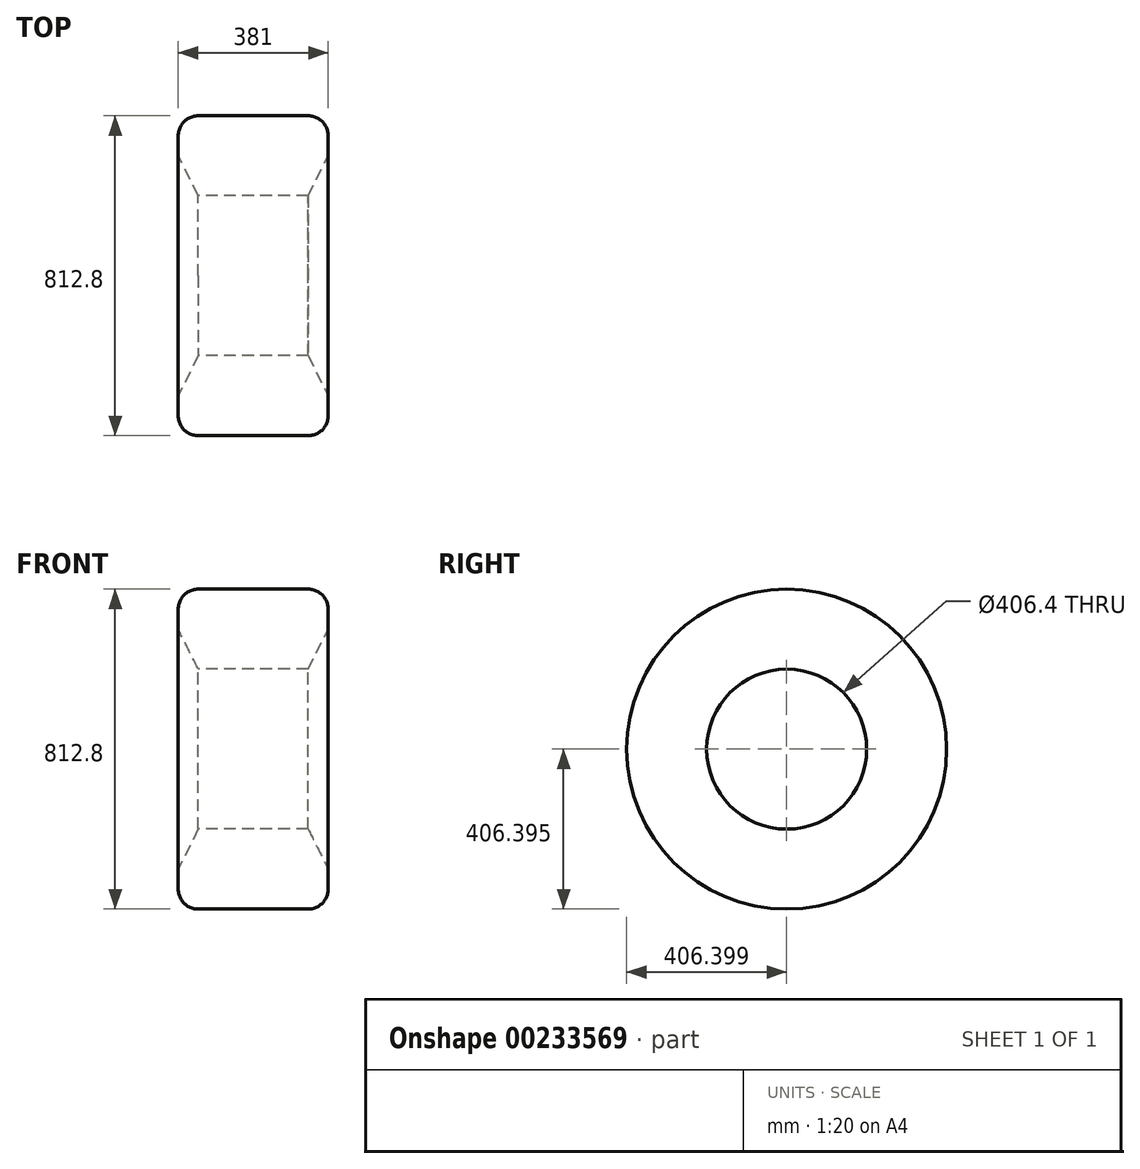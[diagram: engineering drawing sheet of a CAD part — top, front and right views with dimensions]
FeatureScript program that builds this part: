
annotation { "Feature Type Name" : "Feature", "Feature Type Description" : "" }
export const myFeature = defineFeature(function(context is Context, id is Id, definition is map)
    precondition{}
    {
        {
            var Q0;
            Q0=qCreatedBy(makeId("Right.planeOp"),FACE);
            var sketch = newSketch(context, id + "F0", { "sketchPlane" : qUnion([Q0])});
            skCircle(sketch, "E0", {"center": v(-535.52, 357.45) * mm, "radius": 406.4 * mm});
            skCircle(sketch, "E1", {"center": v(-535.52, 357.45) * mm, "radius": 203.2 * mm});
            skLineSegment(sketch, "E2", {"start": v(-535.52, 357.45) * mm, "end": v(-535.52, 763.85) * mm});
            skSolve(sketch);
        }
        {
            var Q0;
            Q0=makeQuery(id+"F0.imprint","IMPRINT",FACE,{"disambiguationData":[TD([[makeQuery(id+"F0.imprint","IMPRINT",EDGE,{"derivedFrom":sQuery(id+"F0.wireOp",EDGE,"E0")}),1.0]])]});
            extrude(context, id + "F1", {"entities" : qUnion([Q0]), "depth" : 381 * mm});
        }
        {
            var Q0;
            Q0=makeQuery(id+"F1.opExtrude","CAP_EDGE",EDGE,{"disambiguationData":[OSD([sQuery(id+"F0.wireOp",EDGE,"E0")])],"isStart":false});
            var Q1;
            Q1=makeQuery(id+"F1.opExtrude","CAP_EDGE",EDGE,{"disambiguationData":[OSD([sQuery(id+"F0.wireOp",EDGE,"E0")])],"isStart":true});
            fillet(context, id + "F2", {"entities" : qUnion([Q0, Q1]), "radius" : 50.8 * mm, "tangentPropagation" : true, "allowEdgeOverflow" : false});
        }
        {
            var Q0;
            Q0=makeQuery(id+"F1.opExtrude","CAP_FACE",FACE,{"disambiguationData":[OSD([sQuery(id+"F0.wireOp",EDGE,"E0"),sQuery(id+"F0.wireOp",EDGE,"E1")])],"isStart":false});
            chamfer(context, id + "F3", {"entities" : qUnion([Q0]), "chamferType" : ChamferType.TWO_OFFSETS, "width1" : 50.8 * mm, "oppositeDirection" : false, "width2" : 101.6 * mm, "tangentPropagation" : true});
        }
        {
            var Q0;
            Q0=makeQuery(id+"F1.opExtrude","CAP_FACE",FACE,{"disambiguationData":[OSD([sQuery(id+"F0.wireOp",EDGE,"E0"),sQuery(id+"F0.wireOp",EDGE,"E1")])],"isStart":true});
            chamfer(context, id + "F4", {"entities" : qUnion([Q0]), "chamferType" : ChamferType.TWO_OFFSETS, "width1" : 101.6 * mm, "oppositeDirection" : false, "width2" : 50.8 * mm, "tangentPropagation" : true});
        }
        {
            var Q0;
            {var subQ0=sQuery(id+"F0.wireOp",EDGE,"E1");Q0=makeQuery(id+"F4.opChamfer","BLEND_EDGE",EDGE,{"blendedFrom":[makeQuery(id+"F1.opExtrude","CAP_EDGE",EDGE,{"disambiguationData":[OSD([subQ0])],"isStart":true}),makeQuery(id+"F1.opExtrude","CAP_FACE",FACE,{"disambiguationData":[OSD([sQuery(id+"F0.wireOp",EDGE,"E0"),subQ0])],"isStart":true})],"blendedInto":[makeQuery(id+"F1.opExtrude","CAP_FACE",FACE,{"disambiguationData":[OSD([sQuery(id+"F0.wireOp",EDGE,"E0"),subQ0])],"isStart":true})]});}
            var Q1;
            {var subQ0=sQuery(id+"F0.wireOp",EDGE,"E0");Q1=makeQuery(id+"F2.opFillet","BLEND_EDGE",EDGE,{"blendedFrom":[makeQuery(id+"F1.opExtrude","CAP_EDGE",EDGE,{"disambiguationData":[OSD([subQ0])],"isStart":true}),makeQuery(id+"F1.opExtrude","CAP_FACE",FACE,{"disambiguationData":[OSD([subQ0,sQuery(id+"F0.wireOp",EDGE,"E1")])],"isStart":true})],"blendedInto":[makeQuery(id+"F1.opExtrude","CAP_FACE",FACE,{"disambiguationData":[OSD([subQ0,sQuery(id+"F0.wireOp",EDGE,"E1")])],"isStart":true})]});}
            var Q2;
            {var subQ0=sQuery(id+"F0.wireOp",EDGE,"E0");Q2=makeQuery(id+"F2.opFillet","BLEND_EDGE",EDGE,{"blendedFrom":[makeQuery(id+"F1.opExtrude","CAP_EDGE",EDGE,{"disambiguationData":[OSD([subQ0])],"isStart":false}),makeQuery(id+"F1.opExtrude","CAP_FACE",FACE,{"disambiguationData":[OSD([subQ0,sQuery(id+"F0.wireOp",EDGE,"E1")])],"isStart":false})],"blendedInto":[makeQuery(id+"F1.opExtrude","CAP_FACE",FACE,{"disambiguationData":[OSD([subQ0,sQuery(id+"F0.wireOp",EDGE,"E1")])],"isStart":false})]});}
            var Q3;
            {var subQ0=sQuery(id+"F0.wireOp",EDGE,"E1");Q3=makeQuery(id+"F3.opChamfer","BLEND_EDGE",EDGE,{"blendedFrom":[makeQuery(id+"F1.opExtrude","CAP_EDGE",EDGE,{"disambiguationData":[OSD([subQ0])],"isStart":false}),makeQuery(id+"F1.opExtrude","CAP_FACE",FACE,{"disambiguationData":[OSD([sQuery(id+"F0.wireOp",EDGE,"E0"),subQ0])],"isStart":false})],"blendedInto":[makeQuery(id+"F1.opExtrude","CAP_FACE",FACE,{"disambiguationData":[OSD([sQuery(id+"F0.wireOp",EDGE,"E0"),subQ0])],"isStart":false})]});}
            fillet(context, id + "F5", {"entities" : qUnion([Q0, Q1, Q2, Q3]), "radius" : 12.7 * mm, "tangentPropagation" : true, "allowEdgeOverflow" : false});
        }
    });
